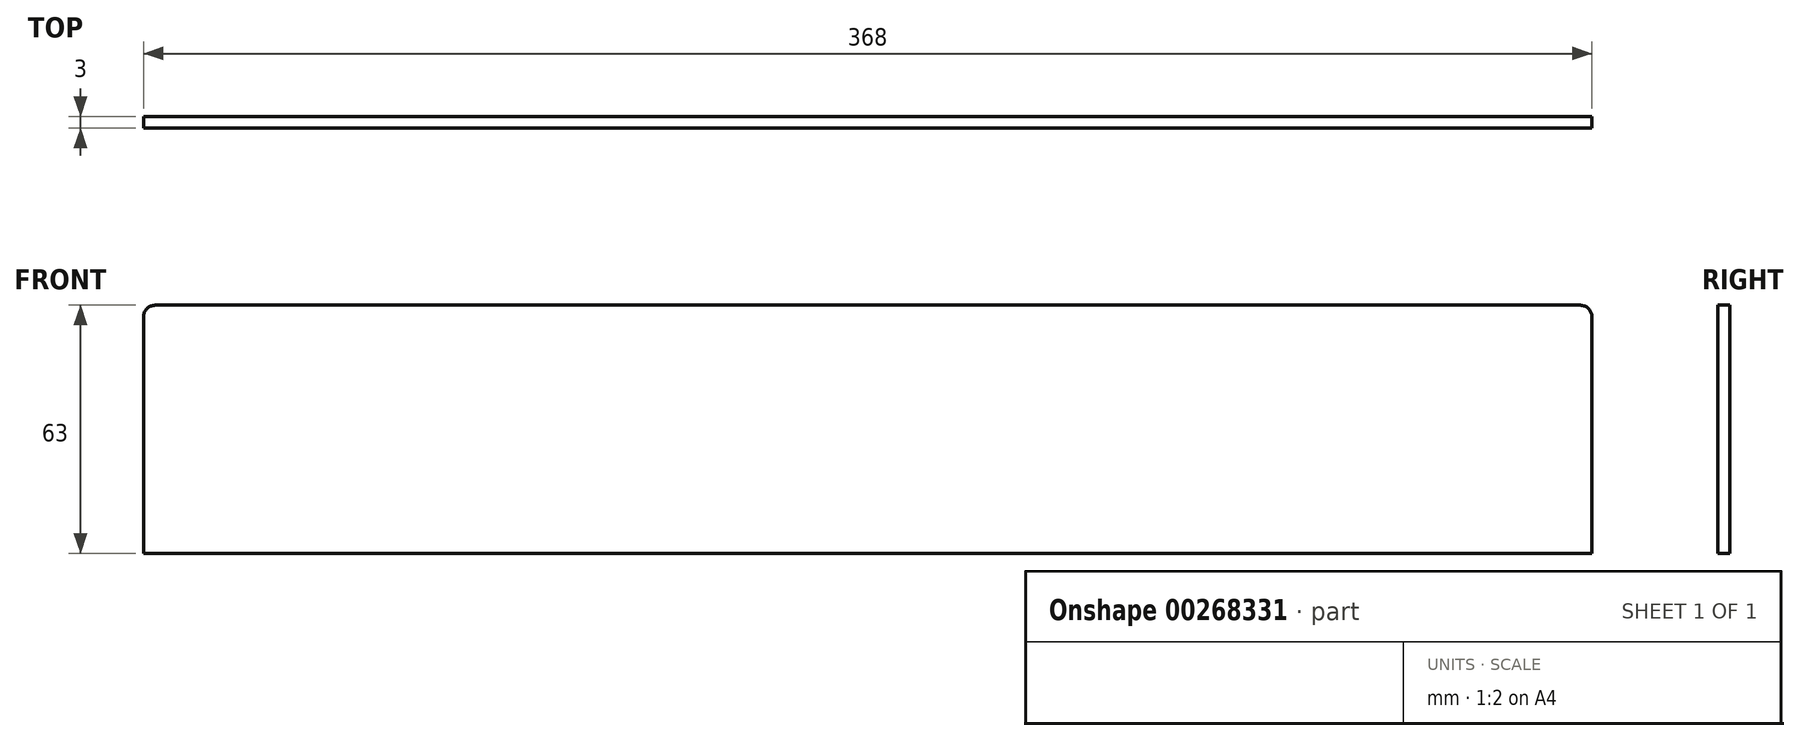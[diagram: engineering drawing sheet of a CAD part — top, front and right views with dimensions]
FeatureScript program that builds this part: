
annotation { "Feature Type Name" : "Feature", "Feature Type Description" : "" }
export const myFeature = defineFeature(function(context is Context, id is Id, definition is map)
    precondition{}
    {
        {
            var Q0;
            Q0=qCreatedBy(makeId("Front.planeOp"),FACE);
            var sketch = newSketch(context, id + "F0", { "sketchPlane" : qUnion([Q0])});
            skLineSegment(sketch, "E0.bottom", {"start": v(-185.79, -51.45) * mm, "end": v(176.21, -51.45) * mm});
            skLineSegment(sketch, "E0.top", {"start": v(-188.79, -114.45) * mm, "end": v(179.21, -114.45) * mm});
            skLineSegment(sketch, "E0.left", {"start": v(-188.79, -54.45) * mm, "end": v(-188.79, -114.45) * mm});
            skLineSegment(sketch, "E0.right", {"start": v(179.21, -54.45) * mm, "end": v(179.21, -114.45) * mm});
            skPoint(sketch, "E1.visualSharp", {"position": v(-188.79, -51.45) * mm});
            skArc(sketch, "E1.filletArc", {"start": v(-185.79, -51.45) * mm, "mid": v(-187.9, -52.33) * mm, "end": v(-188.79, -54.45) * mm});
            skPoint(sketch, "E2.visualSharp", {"position": v(179.21, -51.45) * mm});
            skArc(sketch, "E2.filletArc", {"start": v(179.21, -54.45) * mm, "mid": v(178.33, -52.33) * mm, "end": v(176.21, -51.45) * mm});
            skPoint(sketch, "E3.centerSnap0", {"position": v(179.21, -84.45) * mm});
            skSolve(sketch);
        }
        {
            var Q0;
            Q0=qSketchRegion(id+"F0",true);
            extrude(context, id + "F1", {"entities" : qUnion([Q0]), "depth" : 3 * mm});
        }
    });
